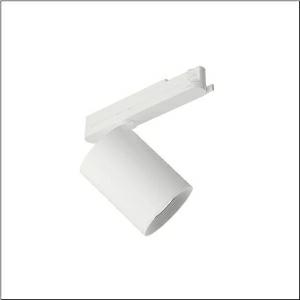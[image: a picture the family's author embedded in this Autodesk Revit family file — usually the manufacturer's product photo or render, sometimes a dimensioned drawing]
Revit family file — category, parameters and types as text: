
# Revit family: spot_21_51se13dba5b
name_source: partatom
category: Lighting Fixtures
units: mm (PartAtom-declared; Revit-internal decimal feet)

## family parameters
Cut with Voids When Loaded = No
Host = Face
Light Source = No
Part Type = Normal
Room Calculation Point = No
Round Connector Dimension = Use Diameter
Shared = No

## types (1)
- --- (1 x LED, 5190 lm, 42.4 W, 2700K)
    Apparent Load = 42 VA
    CIE Flux Codes = 95 98 99 100 100
    Color Rendering = 90
    Color Temperature = 2700K
    Default Elevation = 1800 mm
    Description = Spot 21, directional spotlight, light control with lens, of PMMA, LED rated luminous flux: 4.960lm, light colour: 927, control gear: ECG Multilumen, with 3-phase adapter, mains connection: 220..240V, AC, 50/60Hz, of aluminium, traffic white (RAL 9016), length: 253mm, diameter: 105mm, protection rating (complete): IP20, insulation class (complete): insulation class I (protective earthing), certification: CE, impact resistance: IK02, permissible ambient temperature for indoor applications: -20..+40°C, packaging unit: 1 piece
    Height = 175 mm
    Lamp = 1 x LED
    Lamp Light Flux = 5190 lm
    Lamp Power = 42.4 W
    Lamp count = 1
    Length = 105 mm
    Luminous efficacy = 122 lm/W
    Manufacturer = Siteco
    ModVariant = No
    Model = 51SE13DBA5B
    Mounting Place = Ceiling
    Mounting Type = Pendant
    Number of Poles = 1
    OnlyDefault = Yes
    Power Factor = 1
    Product Name = Spot 21
    Product group = directional spotlight
    ProductGroupID = 904
    Protection Class = Protection class I
    Protection Degree = IP 20
    RLX_Detail_Level = 1
    RlxData = <blob elided: 17589 chars, md5=9d8ddf0b>
    Socket = socket
    Standby Power = 0 W
    System Light Flux = 5190 lm
    System Power = 42 W
    Type Comments = factory setting: luminous flux: 100 % | (ON | ON | ON | ON) | 1050 mA
    Type Image = l_1003976.jpg
    URL = http://relux.com
    VarID = @adj_052925
    Voltage = 0 V
    Weight = 0.00 kg
    Width = 0 mm  [stored 0 ft]

note: [stored X ft] marks values corroborated as IEEE doubles in the binary element streams (Revit-internal decimal feet)

## geometry (parser evidence)
native form markers: Blend x4, Sweep x12
no freeform markers — native parametric forms only
